# Revit family: UM301PR Banco Citizen Eco
name_source: partatom
category: Mobiliario
revit_build: Autodesk Revit 2016 (Build: 20150220_1215(x64)
units: mm (PartAtom-declared; Revit-internal decimal feet)

## family parameters
Compartido = No
Corte con vacíos al cargar = No
Número OmniClass = 23.40.20.00
Punto de cálculo de habitación = No
Se basa en plano de trabajo = No
Siempre vertical = Sí
Título OmniClass = General Furniture and Specialties

## types (1)
- UM301PR Banco Citizen Eco
    Accessibilidad = Sí
    Altura asiento = 450 mm  [stored 1.47638 ft]
    Altura total = 820 mm  [stored 2.69029 ft]
    Ancho = 650 mm  [stored 2.13255 ft]
    Comentarios de tipo = Banco fabricado en polímero reciclado y reciclable, recuperado de la fracción de envases de la recogida selectiva. Asiento y
respaldo en tablón rebnew de 110x40x1800, bancada con apoyabrazos fabricada en polímero inyectado a alta presión, con acabado
marson. No requiere mantenimiento, no se astilla ni se agrieta, tampoco se pudre ni se reseca. Resistente a la humedad. Alta
resistencia a las inclemencias. Tornillería en acero inoxidable.
    Fabricante = BENITO
    Ficha tecnica = http://www.benito.com
    Instalación = Fijación mediante cuatro pernos Ø10, no suministrados.
    Largo = 1800 mm  [stored 5.90551 ft]
    Material bancada = Polímero reciclado ReBnew.
    Material listones = Polímero reciclado ReBnew.
    Modelo = Banco Citizen Eco
    Referencia = UM301PR
    URL = http://www.benito.com
    URL Producto = http://www.benito.com

note: [stored X ft] marks values corroborated as IEEE doubles in the binary element streams (Revit-internal decimal feet)

## geometry (parser evidence)
native form markers: Blend x4
no freeform markers — native parametric forms only
